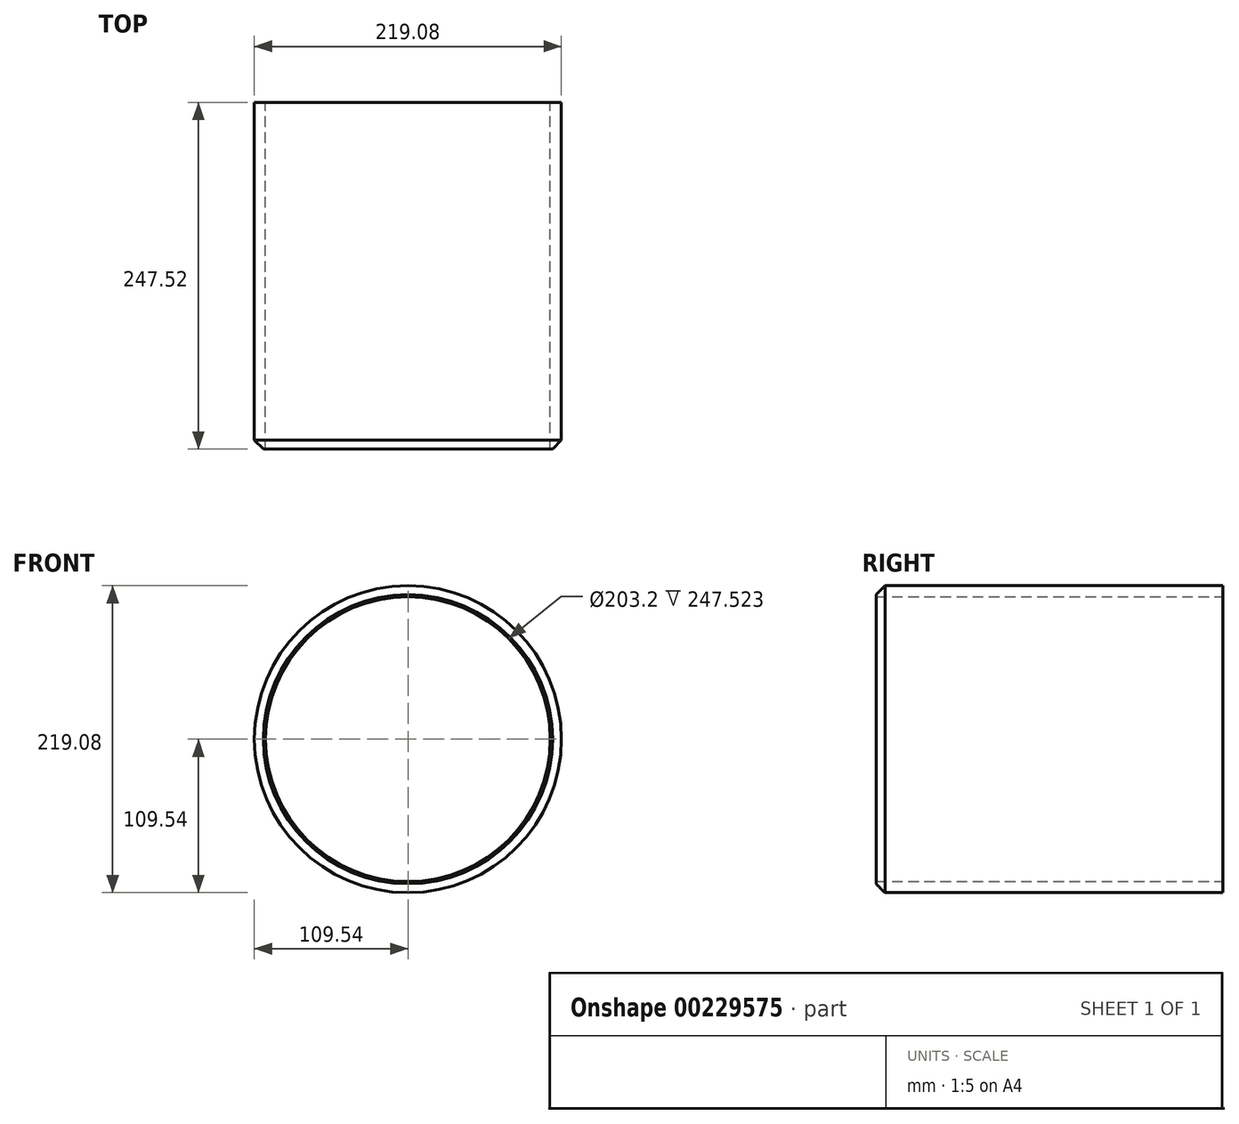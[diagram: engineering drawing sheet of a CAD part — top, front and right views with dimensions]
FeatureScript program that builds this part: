
annotation { "Feature Type Name" : "Feature", "Feature Type Description" : "" }
export const myFeature = defineFeature(function(context is Context, id is Id, definition is map)
    precondition{}
    {
        {
            var Q0;
            Q0=qCreatedBy(makeId("Front.planeOp"),FACE);
            var sketch = newSketch(context, id + "F0", { "sketchPlane" : qUnion([Q0])});
            skCircle(sketch, "E0", {"center": v(0, 0) * mm, "radius": 109.54 * mm});
            skCircle(sketch, "E1", {"center": v(0, 0) * mm, "radius": 101.6 * mm});
            skSolve(sketch);
        }
        {
            var Q0;
            Q0=qSketchRegion(id+"F0",true);
            extrude(context, id + "F1", {"entities" : qUnion([Q0]), "depth" : 247.52 * mm});
        }
        {
            var Q0;
            Q0=makeQuery(id+"F1.opExtrude","CAP_EDGE",EDGE,{"disambiguationData":[OSD([sQuery(id+"F0.wireOp",EDGE,"E0")])],"isStart":false});
            chamfer(context, id + "F2", {"entities" : qUnion([Q0]), "width" : 6.35 * mm, "tangentPropagation" : true});
        }
    });
